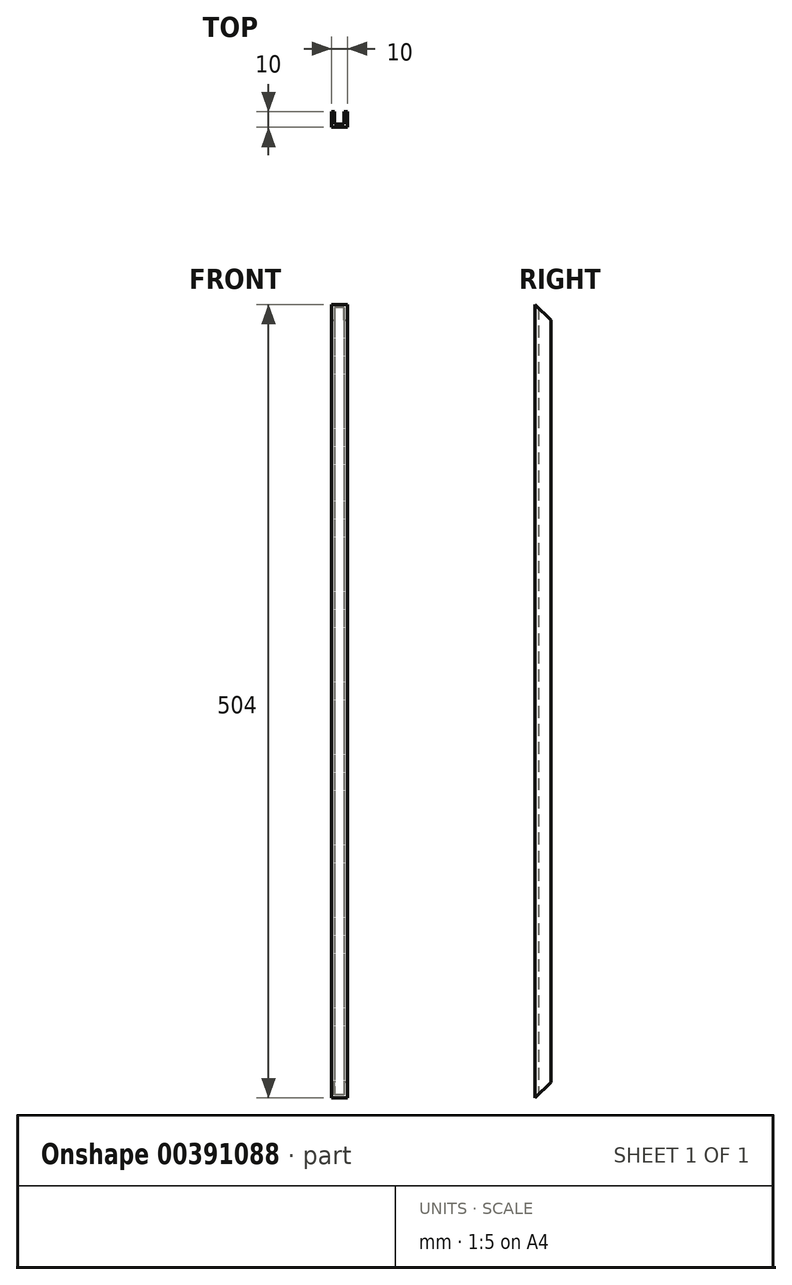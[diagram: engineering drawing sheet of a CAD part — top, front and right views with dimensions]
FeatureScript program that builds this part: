
annotation { "Feature Type Name" : "Feature", "Feature Type Description" : "" }
export const myFeature = defineFeature(function(context is Context, id is Id, definition is map)
    precondition{}
    {
        {
            var Q0;
            Q0=qCreatedBy(makeId("Top.planeOp"),FACE);
            var sketch = newSketch(context, id + "F0", { "sketchPlane" : qUnion([Q0])});
            skLineSegment(sketch, "E0.bottom", {"start": v(-5, 5) * mm, "end": v(5, 5) * mm});
            skLineSegment(sketch, "E0.top", {"start": v(-5, -5) * mm, "end": v(5, -5) * mm});
            skLineSegment(sketch, "E0.left", {"start": v(-5, 5) * mm, "end": v(-5, -5) * mm});
            skLineSegment(sketch, "E0.right", {"start": v(5, 5) * mm, "end": v(5, -5) * mm});
            skPoint(sketch, "E0.middle", {"position": v(0, 0) * mm});
            skLineSegment(sketch, "E1.bottom", {"start": v(-3, 3) * mm, "end": v(3, 3) * mm, "construction": true});
            skLineSegment(sketch, "E1.top", {"start": v(-3, -3) * mm, "end": v(3, -3) * mm, "construction": true});
            skLineSegment(sketch, "E1.left", {"start": v(-3, 3) * mm, "end": v(-3, -3) * mm, "construction": true});
            skLineSegment(sketch, "E1.right", {"start": v(3, 3) * mm, "end": v(3, -3) * mm, "construction": true});
            skLineSegment(sketch, "E2.bottom", {"start": v(-3, -3) * mm, "end": v(3, -3) * mm});
            skLineSegment(sketch, "E2.top", {"start": v(-3, 5) * mm, "end": v(3, 5) * mm});
            skLineSegment(sketch, "E2.left", {"start": v(-3, -3) * mm, "end": v(-3, 5) * mm});
            skLineSegment(sketch, "E2.right", {"start": v(3, -3) * mm, "end": v(3, 5) * mm});
            skSolve(sketch);
        }
        {
            var Q0;
            Q0=makeQuery(id+"F0.imprint","IMPRINT",FACE,{"disambiguationData":[TD([[makeQuery(id+"F0.imprint","IMPRINT",EDGE,{"derivedFrom":sQuery(id+"F0.wireOp",EDGE,"E0.top")}),1.0]])]});
            extrude(context, id + "F1", {"entities" : qUnion([Q0]), "depth" : 504 * mm});
        }
        {
            var Q0;
            {var subQ0=sQuery(id+"F0.wireOp",EDGE,"E0.bottom");Q0=makeQuery(id+"F1.opExtrude","CAP_EDGE",EDGE,{"disambiguationData":[OSD([subQ0]),TDD([makeQuery(id+"F0.imprint","IMPRINT",EDGE,{"disambiguationData":[TD([[makeQuery(id+"F0.imprint","INTERSECT",VERTEX,{"derivedFrom":[subQ0,sQuery(id+"F0.wireOp",EDGE,"E0.left")]}),-1.0]])],"derivedFrom":subQ0})])],"isStart":false});}
            var Q1;
            {var subQ0=sQuery(id+"F0.wireOp",EDGE,"E0.bottom");Q1=makeQuery(id+"F1.opExtrude","CAP_EDGE",EDGE,{"disambiguationData":[OSD([subQ0]),TDD([makeQuery(id+"F0.imprint","IMPRINT",EDGE,{"disambiguationData":[TD([[makeQuery(id+"F0.imprint","INTERSECT",VERTEX,{"derivedFrom":[subQ0,sQuery(id+"F0.wireOp",EDGE,"E0.right")]}),1.0]])],"derivedFrom":subQ0})])],"isStart":false});}
            var Q2;
            {var subQ0=sQuery(id+"F0.wireOp",EDGE,"E0.bottom");Q2=makeQuery(id+"F1.opExtrude","CAP_EDGE",EDGE,{"disambiguationData":[OSD([subQ0]),TDD([makeQuery(id+"F0.imprint","IMPRINT",EDGE,{"disambiguationData":[TD([[makeQuery(id+"F0.imprint","INTERSECT",VERTEX,{"derivedFrom":[subQ0,sQuery(id+"F0.wireOp",EDGE,"E0.right")]}),1.0]])],"derivedFrom":subQ0})])],"isStart":true});}
            var Q3;
            {var subQ0=sQuery(id+"F0.wireOp",EDGE,"E0.bottom");Q3=makeQuery(id+"F1.opExtrude","CAP_EDGE",EDGE,{"disambiguationData":[OSD([subQ0]),TDD([makeQuery(id+"F0.imprint","IMPRINT",EDGE,{"disambiguationData":[TD([[makeQuery(id+"F0.imprint","INTERSECT",VERTEX,{"derivedFrom":[subQ0,sQuery(id+"F0.wireOp",EDGE,"E0.left")]}),-1.0]])],"derivedFrom":subQ0})])],"isStart":true});}
            chamfer(context, id + "F2", {"entities" : qUnion([Q0, Q1, Q2, Q3]), "width" : 10 * mm, "tangentPropagation" : true});
        }
    });
